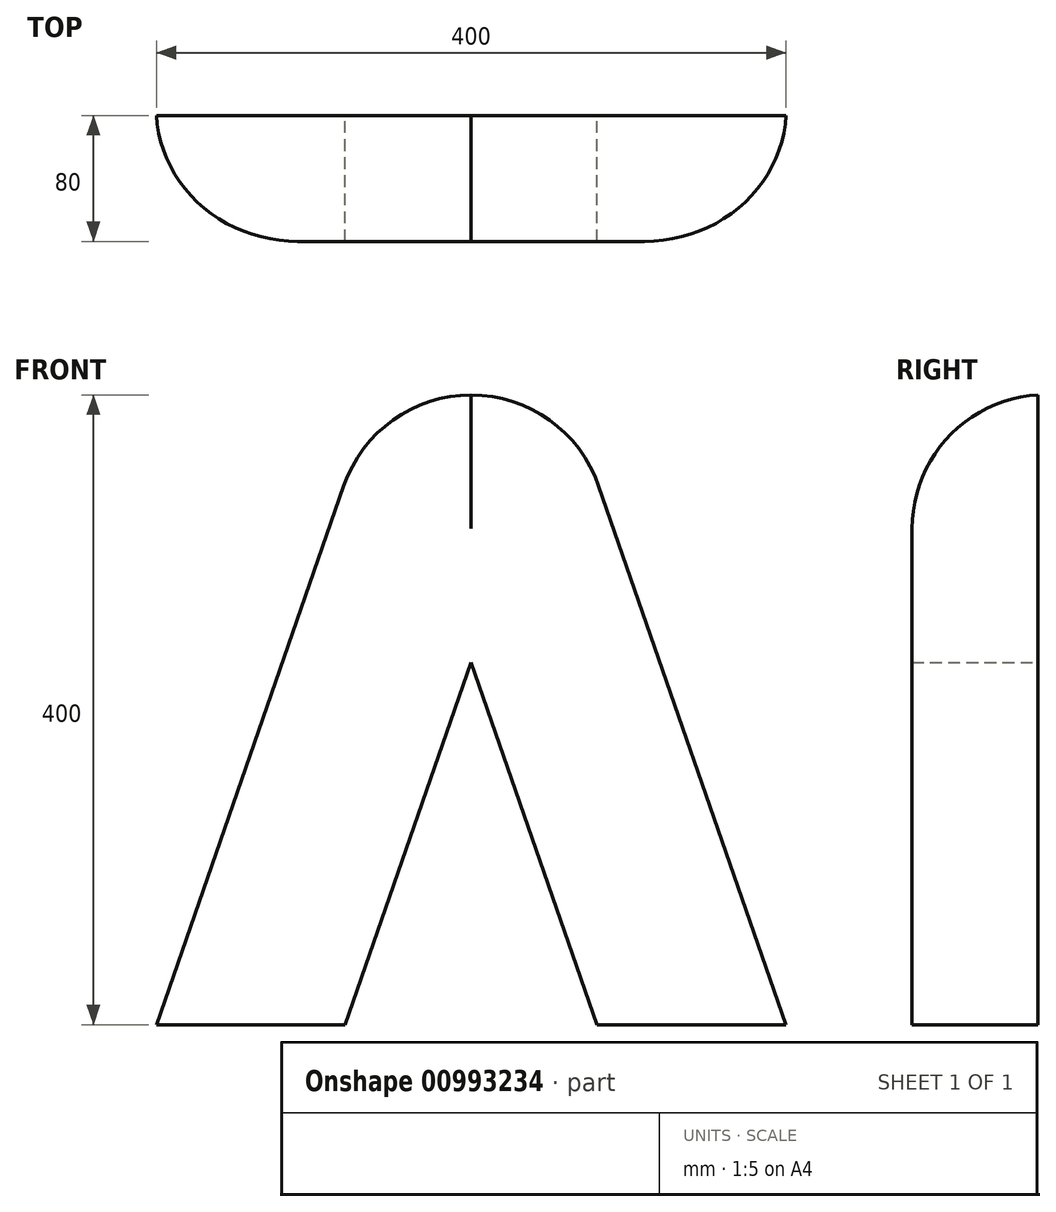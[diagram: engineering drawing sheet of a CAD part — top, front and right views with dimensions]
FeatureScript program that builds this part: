
annotation { "Feature Type Name" : "Feature", "Feature Type Description" : "" }
export const myFeature = defineFeature(function(context is Context, id is Id, definition is map)
    precondition{}
    {
        {
            var Q0;
            Q0=qCreatedBy(makeId("Front.planeOp"),FACE);
            var sketch = newSketch(context, id + "F0", { "sketchPlane" : qUnion([Q0])});
            skLineSegment(sketch, "E0.left", {"start": v(0, 0) * mm, "end": v(0, 0) * mm});
            skLineSegment(sketch, "E0.right", {"start": v(-200, 0) * mm, "end": v(-200, 0) * mm});
            skLineSegment(sketch, "E1.right", {"start": v(200, 0) * mm, "end": v(200, 0) * mm});
            skPoint(sketch, "E2", {"position": v(0, 230) * mm});
            skPoint(sketch, "E3", {"position": v(-100, 230) * mm});
            skPoint(sketch, "E4", {"position": v(100, 230) * mm});
            skLineSegment(sketch, "E5", {"start": v(-80, 0) * mm, "end": v(0, 230) * mm});
            skLineSegment(sketch, "E6", {"start": v(80, 0) * mm, "end": v(0, 230) * mm});
            skLineSegment(sketch, "E7", {"start": v(200, 0) * mm, "end": v(60.87, 400) * mm});
            skLineSegment(sketch, "E8", {"start": v(-200, 0) * mm, "end": v(-60.87, 400) * mm});
            skLineSegment(sketch, "E9", {"start": v(-60.87, 400) * mm, "end": v(60.87, 400) * mm});
            skLineSegment(sketch, "E10", {"start": v(-200, 0) * mm, "end": v(-80, 0) * mm});
            skLineSegment(sketch, "E11", {"start": v(200, 0) * mm, "end": v(80, 0) * mm});
            skSolve(sketch);
        }
        {
            var Q0;
            Q0=makeQuery(id+"F0.imprint","IMPRINT",FACE,{"disambiguationData":[TD([[makeQuery(id+"F0.imprint","IMPRINT",EDGE,{"derivedFrom":sQuery(id+"F0.wireOp",EDGE,"E5")}),1.0]])]});
            extrude(context, id + "F1", {"entities" : qUnion([Q0]), "depth" : 80 * mm, "offsetDistance" : 25 * mm});
        }
        {
            var Q0;
            Q0=makeQuery(id+"F1.opExtrude","SWEPT_EDGE",EDGE,{"disambiguationData":[OSD([sQuery(id+"F0.wireOp",EDGE,"E7"),sQuery(id+"F0.wireOp",EDGE,"E9")])]});
            var Q1;
            Q1=makeQuery(id+"F1.opExtrude","SWEPT_EDGE",EDGE,{"disambiguationData":[OSD([sQuery(id+"F0.wireOp",EDGE,"E8"),sQuery(id+"F0.wireOp",EDGE,"E9")])]});
            fillet(context, id + "F2", {"entities" : qUnion([Q0, Q1]), "radius" : 86 * mm, "tangentPropagation" : true, "allowEdgeOverflow" : false});
        }
        {
            var Q0;
            Q0=makeQuery(id+"F1.opExtrude","CAP_EDGE",EDGE,{"disambiguationData":[OSD([sQuery(id+"F0.wireOp",EDGE,"E7")])],"isStart":false});
            var Q1;
            Q1=makeQuery(id+"F1.opExtrude","CAP_EDGE",EDGE,{"disambiguationData":[OSD([sQuery(id+"F0.wireOp",EDGE,"E8")])],"isStart":false});
            fillet(context, id + "F3", {"entities" : qUnion([Q0, Q1]), "radius" : 85 * mm, "tangentPropagation" : true, "allowEdgeOverflow" : false});
        }
    });
